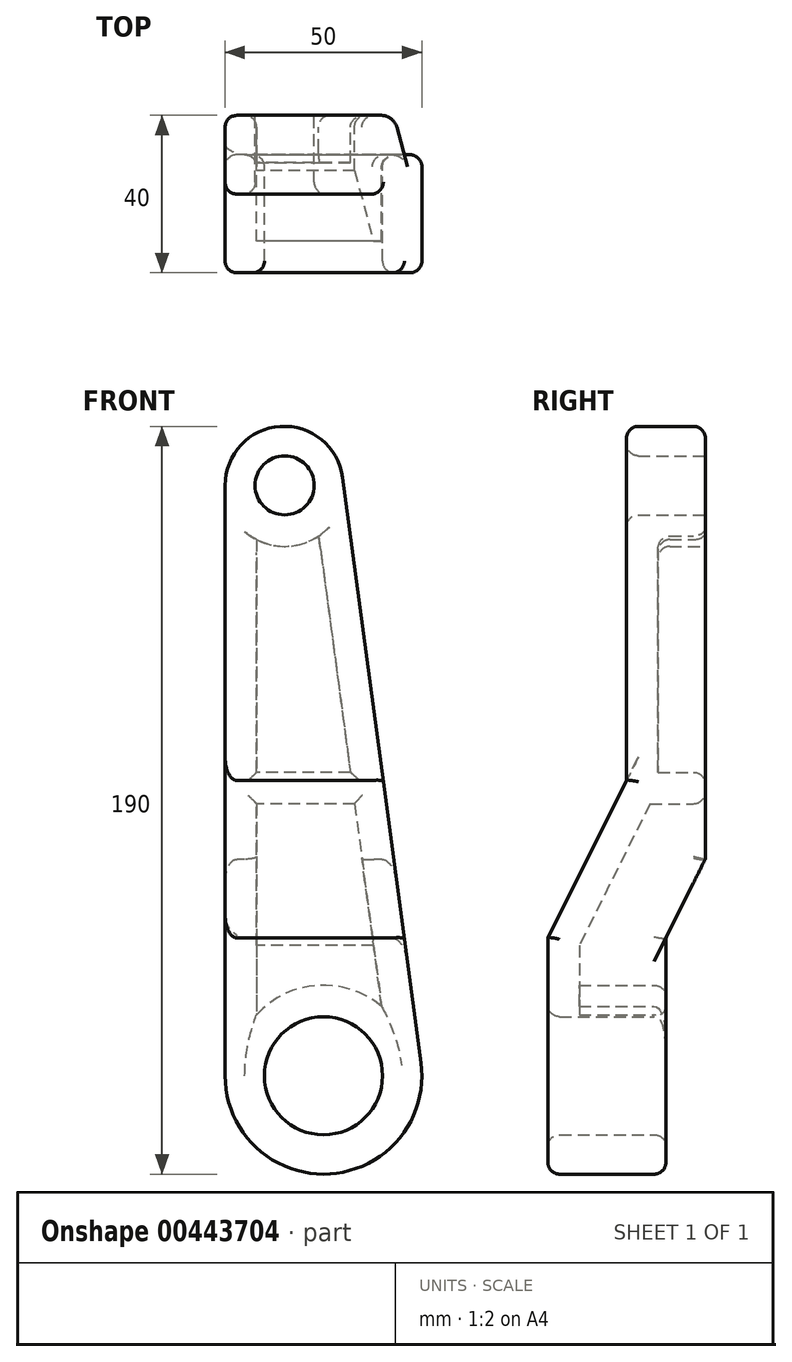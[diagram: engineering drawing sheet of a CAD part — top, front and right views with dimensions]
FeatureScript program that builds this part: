
annotation { "Feature Type Name" : "Feature", "Feature Type Description" : "" }
export const myFeature = defineFeature(function(context is Context, id is Id, definition is map)
    precondition{}
    {
        {
            var Q0;
            Q0=qCreatedBy(makeId("Front.planeOp"),FACE);
            var sketch = newSketch(context, id + "F0", { "sketchPlane" : qUnion([Q0])});
            skCircle(sketch, "E0", {"center": v(0, 0) * mm, "radius": 25 * mm});
            skCircle(sketch, "E1", {"center": v(-10, 150) * mm, "radius": 15 * mm});
            skLineSegment(sketch, "E2", {"start": v(-25, 150) * mm, "end": v(-25, 0) * mm});
            skLineSegment(sketch, "E3", {"start": v(4.87, 152) * mm, "end": v(24.78, 3.32) * mm});
            skSolve(sketch);
        }
        {
            var Q0;
            Q0 = qSketchRegion(id + "F0", true);
            extrude(context, id + "F1", {"entities" : qUnion([Q0]), "depth" : 40 * mm});
        }
        {
            var Q0;
            Q0=makeQuery(id+"F1.opExtrude","SWEPT_FACE",FACE,{"disambiguationData":[OSD([sQuery(id+"F0.wireOp",EDGE,"E2")])]});
            var sketch = newSketch(context, id + "F2", { "sketchPlane" : qUnion([Q0])});
            skLineSegment(sketch, "E4", {"start": v(0, 55) * mm, "end": v(10, 35) * mm});
            skLineSegment(sketch, "E5", {"start": v(10, 35) * mm, "end": v(10, -25.94) * mm});
            skLineSegment(sketch, "E6", {"start": v(0, -25.94) * mm, "end": v(0, 4.26) * mm});
            skLineSegment(sketch, "E7", {"start": v(40, 35) * mm, "end": v(20, 75) * mm});
            skPoint(sketch, "E7.endSnap0", {"position": v(20, 0) * mm});
            skLineSegment(sketch, "E8", {"start": v(20, 75) * mm, "end": v(20, 165.97) * mm});
            skPoint(sketch, "E8.endSnap0", {"position": v(20, 150) * mm});
            skLineSegment(sketch, "E9", {"start": v(40, 165.97) * mm, "end": v(40, 150) * mm});
            skLineSegment(sketch, "E10", {"start": v(40, 150) * mm, "end": v(40, 35) * mm});
            skLineSegment(sketch, "E11", {"start": v(0, -25.94) * mm, "end": v(10, -25.94) * mm});
            skLineSegment(sketch, "E12", {"start": v(20, 165.97) * mm, "end": v(40, 165.97) * mm});
            skSolve(sketch);
        }
        {
            var Q0;
            Q0 = qSketchRegion(id + "F2", true);
            var Q1;
            {var subQ0=sQuery(id+"F2.wireOp",EDGE,"E4");Q1=makeQuery(id+"F2.imprint","IMPRINT",FACE,{"disambiguationData":[TD([[makeQuery(id+"F2.imprint","IMPRINT",EDGE,{"derivedFrom":subQ0}),-1.0]])]});}
            var Q2;
            {var subQ0=sQuery(id+"F2.wireOp",EDGE,"v68NnOcn-07bb-sGXQ-2PtS-IOPSXRDhPe9F");Q2=makeQuery(id+"F2.imprint","IMPRINT",FACE,{"disambiguationData":[TD([[makeQuery(id+"F2.imprint","IMPRINT",EDGE,{"derivedFrom":subQ0}),-1.0]])]});}
            var Q3;
            {var subQ0=sQuery(id+"F2.wireOp",EDGE,"E11");Q3=makeQuery(id+"F2.imprint","IMPRINT",FACE,{"disambiguationData":[TD([[makeQuery(id+"F2.imprint","IMPRINT",EDGE,{"derivedFrom":subQ0}),1.0]])]});}
            extrude(context, id + "F3", {"entities" : qUnion([Q0, Q1, Q2, Q3]), "operationType" : NewBodyOperationType.REMOVE, "endBound" : BoundingType.THROUGH_ALL, "oppositeDirection" : true, "depth" : 25 * mm});
        }
        {
            var Q0;
            Q0=qCreatedBy(makeId("Front.planeOp"),FACE);
            var sketch = newSketch(context, id + "F4", { "sketchPlane" : qUnion([Q0])});
            skCircle(sketch, "E13", {"center": v(0, 0) * mm, "radius": 15 * mm});
            skCircle(sketch, "E14", {"center": v(-9.87, 150) * mm, "radius": 7.5 * mm});
            skSolve(sketch);
        }
        {
            var Q0;
            Q0=makeQuery(id+"F4.imprint","IMPRINT",FACE,{"disambiguationData":[TD([[makeQuery(id+"F4.imprint","IMPRINT",EDGE,{"derivedFrom":sQuery(id+"F4.wireOp",EDGE,"E14")}),1.0]])]});
            var Q1;
            Q1=makeQuery(id+"F4.imprint","IMPRINT",FACE,{"disambiguationData":[TD([[makeQuery(id+"F4.imprint","IMPRINT",EDGE,{"derivedFrom":sQuery(id+"F4.wireOp",EDGE,"E13")}),1.0]])]});
            extrude(context, id + "F5", {"entities" : qUnion([Q0, Q1]), "operationType" : NewBodyOperationType.REMOVE, "endBound" : BoundingType.THROUGH_ALL, "depth" : 25 * mm});
        }
        {
            var Q0;
            Q0=makeQuery(id+"F1.opExtrude","CAP_FACE",FACE,{"disambiguationData":[OSD([sQuery(id+"F0.wireOp",EDGE,"E0"),sQuery(id+"F0.wireOp",EDGE,"E1"),sQuery(id+"F0.wireOp",EDGE,"E2"),sQuery(id+"F0.wireOp",EDGE,"E3")])],"isStart":true});
            var Q1;
            Q1=makeQuery(id+"F3.boolean.opBoolean","COPY",FACE,{"derivedFrom":makeQuery(id+"F3.opExtrude","SWEPT_FACE",FACE,{"disambiguationData":[OSD([sQuery(id+"F2.wireOp",EDGE,"E4")])]})});
            var Q2;
            Q2=makeQuery(id+"F3.boolean.opBoolean","COPY",FACE,{"derivedFrom":makeQuery(id+"F3.opExtrude","SWEPT_FACE",FACE,{"disambiguationData":[OSD([sQuery(id+"F2.wireOp",EDGE,"E5")])]})});
            shell(context, id + "F6", {"entities" : qUnion([Q0, Q1, Q2]), "thickness" : 8 * mm});
        }
        {
            var Q0;
            Q0=makeQuery(id+"F1.opExtrude","CAP_FACE",FACE,{"disambiguationData":[OSD([sQuery(id+"F0.wireOp",EDGE,"E0"),sQuery(id+"F0.wireOp",EDGE,"E1"),sQuery(id+"F0.wireOp",EDGE,"E2"),sQuery(id+"F0.wireOp",EDGE,"E3")])],"isStart":true});
            var sketch = newSketch(context, id + "F7", { "sketchPlane" : qUnion([Q0])});
            skLineSegment(sketch, "E15", {"start": v(-6.82, 77.11) * mm, "end": v(17, 77.11) * mm});
            skLineSegment(sketch, "E16", {"start": v(-7.9, 69.11) * mm, "end": v(17, 69.11) * mm});
            skLineSegment(sketch, "E17.0", {"start": v(-6.82, 77.11) * mm, "end": v(-7.9, 69.11) * mm});
            skLineSegment(sketch, "E17.1", {"start": v(17, 77.11) * mm, "end": v(17, 69.11) * mm});
            skPoint(sketch, "E18.orphan", {"position": v(-9.79, 55) * mm});
            skPoint(sketch, "E19.orphan", {"position": v(1.22, 137.14) * mm});
            skPoint(sketch, "E20.orphan", {"position": v(17, 136.24) * mm});
            skPoint(sketch, "E21.orphan", {"position": v(17, 55) * mm});
            skSolve(sketch);
        }
        {
            var Q0;
            Q0 = qSketchRegion(id + "F7", true);
            extrude(context, id + "F8", {"entities" : qUnion([Q0]), "operationType" : NewBodyOperationType.ADD, "endBound" : BoundingType.UP_TO_NEXT, "oppositeDirection" : true, "depth" : 25 * mm});
        }
        {
            var Q0;
            Q0=makeQuery(id+"F1.opExtrude","CAP_EDGE",EDGE,{"disambiguationData":[OSD([sQuery(id+"F0.wireOp",EDGE,"E1")])],"isStart":true});
            var Q1;
            Q1=makeQuery(id+"F3.boolean.opBoolean","INTERSECT",EDGE,{"derivedFrom":[makeQuery(id+"F1.opExtrude","SWEPT_FACE",FACE,{"disambiguationData":[OSD([sQuery(id+"F0.wireOp",EDGE,"E1")])]}),makeQuery(id+"F3.opExtrude","SWEPT_FACE",FACE,{"disambiguationData":[OSD([sQuery(id+"F2.wireOp",EDGE,"E8")])]})]});
            var Q2;
            Q2=makeQuery(id+"F3.boolean.opBoolean","INTERSECT",EDGE,{"derivedFrom":[makeQuery(id+"F1.opExtrude","SWEPT_FACE",FACE,{"disambiguationData":[OSD([sQuery(id+"F0.wireOp",EDGE,"E3")])]}),makeQuery(id+"F3.opExtrude","SWEPT_FACE",FACE,{"disambiguationData":[OSD([sQuery(id+"F2.wireOp",EDGE,"E7")])]})]});
            var Q3;
            Q3=makeQuery(id+"F3.boolean.opBoolean","COPY",EDGE,{"derivedFrom":makeQuery(id+"F3.opExtrude","CAP_EDGE",EDGE,{"disambiguationData":[OSD([sQuery(id+"F2.wireOp",EDGE,"E7")])],"isStart":true})});
            var Q4;
            Q4=makeQuery(id+"F1.opExtrude","CAP_EDGE",EDGE,{"disambiguationData":[OSD([sQuery(id+"F0.wireOp",EDGE,"E0")])],"isStart":false});
            var Q5;
            Q5=makeQuery(id+"F3.boolean.opBoolean","INTERSECT",EDGE,{"derivedFrom":[makeQuery(id+"F1.opExtrude","SWEPT_FACE",FACE,{"disambiguationData":[OSD([sQuery(id+"F0.wireOp",EDGE,"E0")])]}),makeQuery(id+"F3.opExtrude","SWEPT_FACE",FACE,{"disambiguationData":[OSD([sQuery(id+"F2.wireOp",EDGE,"E5")])]})]});
            var Q6;
            Q6=makeQuery(id+"F6.opShell","OFFSET_EDGE",EDGE,{"disambiguationData":[OSD([sQuery(id+"F2.wireOp",EDGE,"E5"),sQuery(id+"F4.wireOp",EDGE,"E13")])]});
            var Q7;
            Q7=makeQuery(id+"F5.boolean.opBoolean","COPY",EDGE,{"derivedFrom":makeQuery(id+"F5.opExtrude","CAP_EDGE",EDGE,{"disambiguationData":[OSD([sQuery(id+"F4.wireOp",EDGE,"E14")])],"isStart":true})});
            var Q8;
            Q8=makeQuery(id+"F5.boolean.opBoolean","INTERSECT",EDGE,{"derivedFrom":[makeQuery(id+"F3.boolean.opBoolean","COPY",FACE,{"derivedFrom":makeQuery(id+"F3.opExtrude","SWEPT_FACE",FACE,{"disambiguationData":[OSD([sQuery(id+"F2.wireOp",EDGE,"E8")])]})}),makeQuery(id+"F5.opExtrude","SWEPT_FACE",FACE,{"disambiguationData":[OSD([sQuery(id+"F4.wireOp",EDGE,"E14")])]})]});
            var Q9;
            Q9=makeQuery(id+"F5.boolean.opBoolean","INTERSECT",EDGE,{"derivedFrom":[makeQuery(id+"F1.opExtrude","CAP_FACE",FACE,{"disambiguationData":[OSD([sQuery(id+"F0.wireOp",EDGE,"E0"),sQuery(id+"F0.wireOp",EDGE,"E1"),sQuery(id+"F0.wireOp",EDGE,"E2"),sQuery(id+"F0.wireOp",EDGE,"E3")])],"isStart":false}),makeQuery(id+"F5.opExtrude","SWEPT_FACE",FACE,{"disambiguationData":[OSD([sQuery(id+"F4.wireOp",EDGE,"E13")])]})]});
            var Q10;
            Q10=makeQuery(id+"F5.boolean.opBoolean","INTERSECT",EDGE,{"derivedFrom":[makeQuery(id+"F3.boolean.opBoolean","COPY",FACE,{"derivedFrom":makeQuery(id+"F3.opExtrude","SWEPT_FACE",FACE,{"disambiguationData":[OSD([sQuery(id+"F2.wireOp",EDGE,"E5")])]})}),makeQuery(id+"F5.opExtrude","SWEPT_FACE",FACE,{"disambiguationData":[OSD([sQuery(id+"F4.wireOp",EDGE,"E13")])]})]});
            var Q11;
            {var subQ0=sQuery(id+"F0.wireOp",EDGE,"E3");Q11=makeQuery(id+"F8.boolean.opBoolean","SPLIT",EDGE,{"disambiguationData":[TD([makeQuery(id+"F6.opShell","OFFSET_FACE",FACE,{"disambiguationData":[OSD([sQuery(id+"F4.wireOp",EDGE,"E14")])]})])],"derivedFrom":makeQuery(id+"F6.opShell","OFFSET_EDGE",EDGE,{"disambiguationData":[OSD([subQ0]),TDD([makeQuery(id+"F1.opExtrude","CAP_EDGE",EDGE,{"disambiguationData":[OSD([subQ0])],"isStart":true})])]})});}
            var Q12;
            Q12=makeQuery(id+"F6.opShell","OFFSET_EDGE",EDGE,{"disambiguationData":[OSD([sQuery(id+"F4.wireOp",EDGE,"E14")])]});
            var Q13;
            {var subQ0=sQuery(id+"F0.wireOp",EDGE,"E2");Q13=makeQuery(id+"F8.boolean.opBoolean","SPLIT",EDGE,{"disambiguationData":[TD([makeQuery(id+"F6.opShell","OFFSET_FACE",FACE,{"disambiguationData":[OSD([sQuery(id+"F4.wireOp",EDGE,"E14")])]})])],"derivedFrom":makeQuery(id+"F6.opShell","OFFSET_EDGE",EDGE,{"disambiguationData":[OSD([subQ0]),TDD([makeQuery(id+"F1.opExtrude","CAP_EDGE",EDGE,{"disambiguationData":[OSD([subQ0])],"isStart":true})])]})});}
            var Q14;
            Q14=makeQuery(id+"F8.opExtrude","CAP_EDGE",EDGE,{"disambiguationData":[OSD([sQuery(id+"F7.wireOp",EDGE,"E15")])],"isStart":true});
            var Q15;
            {var subQ1=sQuery(id+"F0.wireOp",EDGE,"E3");Q15=makeQuery(id+"F8.boolean.opBoolean","SPLIT",EDGE,{"disambiguationData":[TD([makeQuery(id+"F3.boolean.opBoolean","COPY",FACE,{"derivedFrom":makeQuery(id+"F3.opExtrude","SWEPT_FACE",FACE,{"disambiguationData":[OSD([sQuery(id+"F2.wireOp",EDGE,"E4")])]})})])],"derivedFrom":makeQuery(id+"F6.opShell","OFFSET_EDGE",EDGE,{"disambiguationData":[OSD([subQ1]),TDD([makeQuery(id+"F1.opExtrude","CAP_EDGE",EDGE,{"disambiguationData":[OSD([subQ1])],"isStart":true})])]})});}
            var Q16;
            Q16=makeQuery(id+"F8.opExtrude","CAP_EDGE",EDGE,{"disambiguationData":[OSD([sQuery(id+"F7.wireOp",EDGE,"E16")])],"isStart":true});
            var Q17;
            {var subQ1=sQuery(id+"F0.wireOp",EDGE,"E2");Q17=makeQuery(id+"F8.boolean.opBoolean","SPLIT",EDGE,{"disambiguationData":[TD([makeQuery(id+"F6.opShell","OFFSET_FACE",FACE,{"disambiguationData":[OSD([sQuery(id+"F2.wireOp",EDGE,"E4")])]})])],"derivedFrom":makeQuery(id+"F6.opShell","OFFSET_EDGE",EDGE,{"disambiguationData":[OSD([subQ1]),TDD([makeQuery(id+"F1.opExtrude","CAP_EDGE",EDGE,{"disambiguationData":[OSD([subQ1])],"isStart":true})])]})});}
            var Q18;
            Q18=makeQuery(id+"F6.opShell","OFFSET_EDGE",EDGE,{"disambiguationData":[OSD([sQuery(id+"F2.wireOp",EDGE,"E4")])]});
            var Q19;
            Q19=makeQuery(id+"F6.opShell","OFFSET_EDGE",EDGE,{"disambiguationData":[OSD([sQuery(id+"F0.wireOp",EDGE,"E3"),sQuery(id+"F2.wireOp",EDGE,"E4")])]});
            var Q20;
            Q20=makeQuery(id+"F6.opShell","OFFSET_EDGE",EDGE,{"disambiguationData":[OSD([sQuery(id+"F0.wireOp",EDGE,"E3"),sQuery(id+"F2.wireOp",EDGE,"E5")])]});
            var Q21;
            Q21=makeQuery(id+"F6.opShell","OFFSET_EDGE",EDGE,{"disambiguationData":[OSD([sQuery(id+"F2.wireOp",EDGE,"E5")])]});
            fillet(context, id + "F9", {"entities" : qUnion([Q0, Q1, Q2, Q3, Q4, Q5, Q6, Q7, Q8, Q9, Q10, Q11, Q12, Q13, Q14, Q15, Q16, Q17, Q18, Q19, Q20, Q21]), "radius" : 3 * mm, "tangentPropagation" : true, "allowEdgeOverflow" : false});
        }
    });
